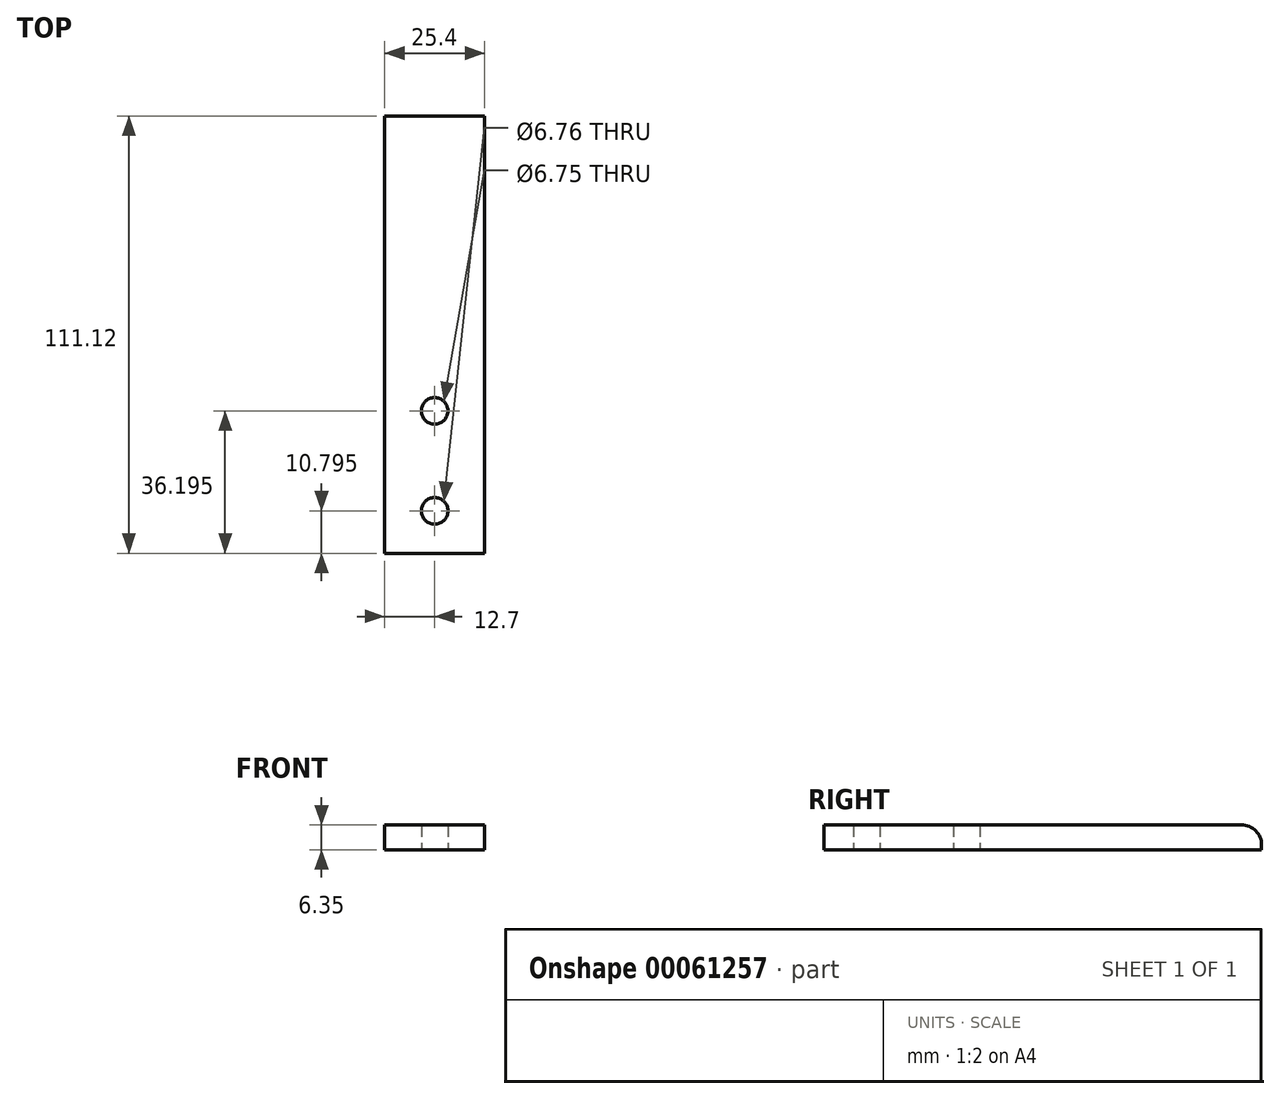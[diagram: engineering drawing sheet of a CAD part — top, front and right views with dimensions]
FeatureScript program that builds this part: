
annotation { "Feature Type Name" : "Feature", "Feature Type Description" : "" }
export const myFeature = defineFeature(function(context is Context, id is Id, definition is map)
    precondition{}
    {
        {
            var Q0;
            Q0=qCreatedBy(makeId("Top.planeOp"),FACE);
            var sketch = newSketch(context, id + "F0", { "sketchPlane" : qUnion([Q0])});
            skLineSegment(sketch, "E0.bottom", {"start": v(0, 0) * mm, "end": v(25.4, 0) * mm});
            skLineSegment(sketch, "E0.top", {"start": v(0, 111.13) * mm, "end": v(25.4, 111.13) * mm});
            skLineSegment(sketch, "E0.left", {"start": v(0, 0) * mm, "end": v(0, 111.13) * mm});
            skLineSegment(sketch, "E0.right", {"start": v(25.4, 0) * mm, "end": v(25.4, 111.13) * mm});
            skCircle(sketch, "E1", {"center": v(12.7, 10.8) * mm, "radius": 3.38 * mm});
            skCircle(sketch, "E2", {"center": v(12.7, 36.2) * mm, "radius": 3.37 * mm});
            skSolve(sketch);
        }
        {
            var Q0;
            Q0=makeQuery(id+"F0.imprint","IMPRINT",FACE,{"disambiguationData":[TD([[makeQuery(id+"F0.imprint","IMPRINT",EDGE,{"derivedFrom":sQuery(id+"F0.wireOp",EDGE,"E0.bottom")}),1.0]])]});
            extrude(context, id + "F1", {"entities" : qUnion([Q0]), "depth" : 6.35 * mm});
        }
        {
            var Q0;
            Q0=makeQuery(id+"F1.opExtrude","CAP_EDGE",EDGE,{"disambiguationData":[OSD([sQuery(id+"F0.wireOp",EDGE,"E0.top")])],"isStart":false});
            fillet(context, id + "F2", {"entities" : qUnion([Q0]), "radius" : 5.08 * mm, "tangentPropagation" : true, "allowEdgeOverflow" : false});
        }
    });
